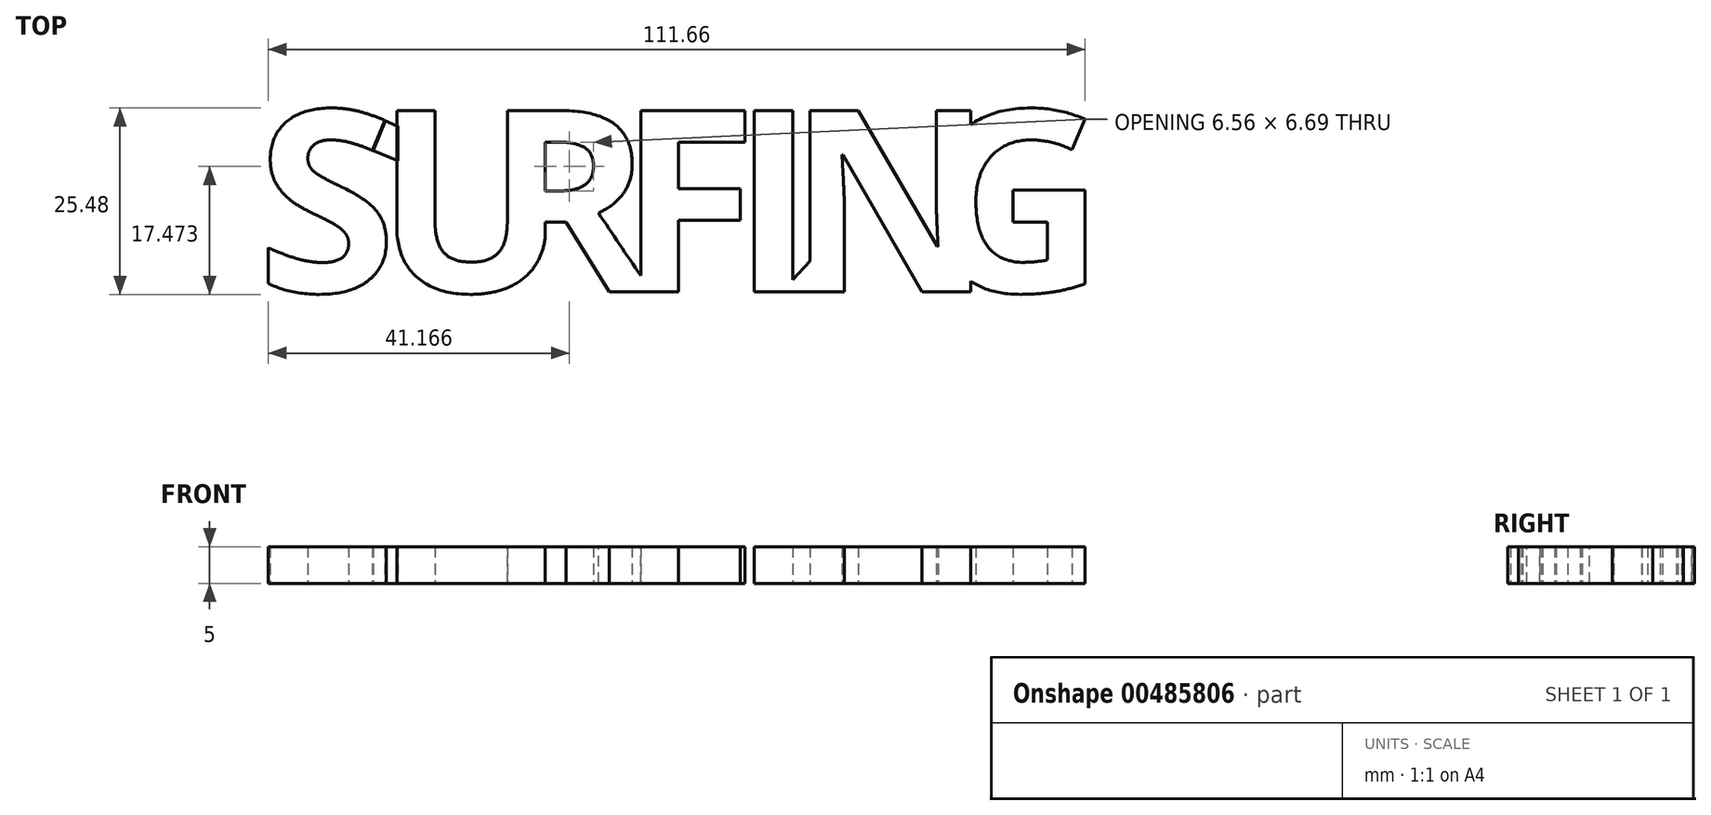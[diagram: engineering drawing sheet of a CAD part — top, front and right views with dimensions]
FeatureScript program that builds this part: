
annotation { "Feature Type Name" : "Feature", "Feature Type Description" : "" }
export const myFeature = defineFeature(function(context is Context, id is Id, definition is map)
    precondition{}
    {
        {
            var Q0;
            Q0=qCreatedBy(makeId("Top.planeOp"),FACE);
            var sketch = newSketch(context, id + "F0", { "sketchPlane" : qUnion([Q0])});
            skText(sketch, "E0", { "text": "S", "fontName": "NotoSans-Bold.ttf"});
            skText(sketch, "E1", { "text": "U", "fontName": "OpenSans-Bold.ttf"});
            skText(sketch, "E2", { "text": "R", "fontName": "OpenSans-Bold.ttf"});
            skText(sketch, "E3", { "text": "F", "fontName": "OpenSans-Bold.ttf"});
            skText(sketch, "E4", { "text": "I", "fontName": "OpenSans-Bold.ttf"});
            skText(sketch, "E5", { "text": "N", "fontName": "OpenSans-Bold.ttf"});
            skText(sketch, "E6", { "text": "G", "fontName": "OpenSans-Bold.ttf"});
            skLineSegment(sketch, "E7", {"start": v(-42.43, 23.41) * mm, "end": v(-40.7, 22.65) * mm});
            skLineSegment(sketch, "E8", {"start": v(-40.7, 22.65) * mm, "end": v(-40.7, 17.93) * mm});
            skLineSegment(sketch, "E9", {"start": v(-40.7, 17.93) * mm, "end": v(-44.15, 19.35) * mm});
            skLineSegment(sketch, "E10", {"start": v(-44.15, 19.35) * mm, "end": v(-42.43, 23.41) * mm});
            skLineSegment(sketch, "E11", {"start": v(6.74, 24.79) * mm, "end": v(10.2, 24.79) * mm});
            skLineSegment(sketch, "E12", {"start": v(10.2, 24.79) * mm, "end": v(6.74, 20.48) * mm});
            skLineSegment(sketch, "E13", {"start": v(6.74, 20.48) * mm, "end": v(6.74, 24.79) * mm});
            skLineSegment(sketch, "E14", {"start": v(15.66, 4.2) * mm, "end": v(11.68, 0) * mm});
            skLineSegment(sketch, "E15", {"start": v(11.68, 0) * mm, "end": v(16.34, 0) * mm});
            skLineSegment(sketch, "E16", {"start": v(16.34, 0) * mm, "end": v(20.31, 4.2) * mm});
            skLineSegment(sketch, "E17", {"start": v(20.31, 4.2) * mm, "end": v(15.66, 4.2) * mm});
            const initialGuessF0  = {"E0": [-0.06, 0, 1, 0, 0.025], "E1": [-0.04377, 0, 1, 0, 0.025], "E2": [-0.02889, 0, 1, 0, 0.025], "E3": [-0.0106, 0, 1, 0, 0.025], "E4": [0.00489, 0, 1, 0, 0.025], "E5": [0.01252, 0, 1, 0, 0.025], "E6": [0.0309, 0, 1, 0, 0.025]};
            skSetInitialGuess(sketch, initialGuessF0);
            skSolve(sketch);
        }
        {
            var Q0;
            Q0=makeQuery(id+"F0.imprint","IMPRINT",FACE,{"disambiguationData":[TD([[makeQuery(id+"F0.imprint","IMPRINT",EDGE,{"derivedFrom":sQuery(id+"F0.wireOp",EDGE,"E0.sketch_text.stroke-0")}),-1.0]])]});
            var Q1;
            {var subQ0=sQuery(id+"F0.wireOp",EDGE,"E7");var subQ1=sQuery(id+"F0.wireOp",EDGE,"E0.sketch_text.stroke-18");var subQ2=makeQuery(id+"F0.imprint","INTERSECT",VERTEX,{"derivedFrom":[subQ1,subQ0]});Q1=makeQuery(id+"F0.imprint","IMPRINT",FACE,{"disambiguationData":[TD([[makeQuery(id+"F0.imprint","IMPRINT",EDGE,{"disambiguationData":[TD([[subQ2,-1.0]])],"derivedFrom":subQ1}),1.0]])]});}
            var Q2;
            {var subQ6=sQuery(id+"F0.wireOp",EDGE,"E1.sketch_text.stroke-4");Q2=makeQuery(id+"F0.imprint","IMPRINT",FACE,{"disambiguationData":[TD([[makeQuery(id+"F0.imprint","IMPRINT",EDGE,{"derivedFrom":subQ6}),-1.0]])]});}
            var Q3;
            {var subQ2=sQuery(id+"F0.wireOp",EDGE,"E1.sketch_text.stroke-2");Q3=makeQuery(id+"F0.imprint","IMPRINT",FACE,{"disambiguationData":[TD([[makeQuery(id+"F0.imprint","IMPRINT",EDGE,{"derivedFrom":subQ2}),-1.0]])]});}
            var Q4;
            {var subQ12=sQuery(id+"F0.wireOp",EDGE,"E2.sketch_text.stroke-1");Q4=makeQuery(id+"F0.imprint","IMPRINT",FACE,{"disambiguationData":[TD([[makeQuery(id+"F0.imprint","IMPRINT",EDGE,{"derivedFrom":subQ12}),-1.0]])]});}
            var Q5;
            {var subQ9=sQuery(id+"F0.wireOp",EDGE,"E3.sketch_text.stroke-2");Q5=makeQuery(id+"F0.imprint","IMPRINT",FACE,{"disambiguationData":[TD([[makeQuery(id+"F0.imprint","IMPRINT",EDGE,{"derivedFrom":subQ9}),-1.0]])]});}
            var Q6;
            {var subQ0=sQuery(id+"F0.wireOp",EDGE,"E3.sketch_text.stroke-0");var subQ1=sQuery(id+"F0.wireOp",EDGE,"E2.sketch_text.stroke-15");var subQ2=makeQuery(id+"F0.imprint","INTERSECT",VERTEX,{"derivedFrom":[subQ1,subQ0]});Q6=makeQuery(id+"F0.imprint","IMPRINT",FACE,{"disambiguationData":[TD([[makeQuery(id+"F0.imprint","IMPRINT",EDGE,{"disambiguationData":[TD([[subQ2,1.0]])],"derivedFrom":subQ1}),-1.0]])]});}
            var Q7;
            {var subQ0=sQuery(id+"F0.wireOp",EDGE,"E11");var subQ1=sQuery(id+"F0.wireOp",EDGE,"E3.sketch_text.stroke-3");var subQ2=makeQuery(id+"F0.imprint","INTERSECT",VERTEX,{"derivedFrom":[subQ1,subQ0]});Q7=makeQuery(id+"F0.imprint","IMPRINT",FACE,{"disambiguationData":[TD([[makeQuery(id+"F0.imprint","IMPRINT",EDGE,{"disambiguationData":[TD([[subQ2,-1.0]])],"derivedFrom":subQ1}),1.0]])]});}
            var Q8;
            {var subQ1=sQuery(id+"F0.wireOp",EDGE,"E4.sketch_text.stroke-1");Q8=makeQuery(id+"F0.imprint","IMPRINT",FACE,{"disambiguationData":[TD([[makeQuery(id+"F0.imprint","IMPRINT",EDGE,{"derivedFrom":subQ1}),-1.0]])]});}
            var Q9;
            {var subQ0=sQuery(id+"F0.wireOp",EDGE,"E11");var subQ1=sQuery(id+"F0.wireOp",EDGE,"E4.sketch_text.stroke-0");var subQ2=makeQuery(id+"F0.imprint","INTERSECT",VERTEX,{"derivedFrom":[subQ1,subQ0]});Q9=makeQuery(id+"F0.imprint","IMPRINT",FACE,{"disambiguationData":[TD([[makeQuery(id+"F0.imprint","IMPRINT",EDGE,{"disambiguationData":[TD([[subQ2,1.0]])],"derivedFrom":subQ1}),-1.0]])]});}
            var Q10;
            {var subQ0=sQuery(id+"F0.wireOp",EDGE,"E15");var subQ1=sQuery(id+"F0.wireOp",EDGE,"E4.sketch_text.stroke-2");var subQ2=makeQuery(id+"F0.imprint","INTERSECT",VERTEX,{"derivedFrom":[subQ1,subQ0]});Q10=makeQuery(id+"F0.imprint","IMPRINT",FACE,{"disambiguationData":[TD([[makeQuery(id+"F0.imprint","IMPRINT",EDGE,{"disambiguationData":[TD([[subQ2,1.0]])],"derivedFrom":subQ1}),1.0]])]});}
            var Q11;
            {var subQ0=sQuery(id+"F0.wireOp",EDGE,"E15");var subQ1=sQuery(id+"F0.wireOp",EDGE,"E4.sketch_text.stroke-2");var subQ2=makeQuery(id+"F0.imprint","INTERSECT",VERTEX,{"derivedFrom":[subQ1,subQ0]});Q11=makeQuery(id+"F0.imprint","IMPRINT",FACE,{"disambiguationData":[TD([[makeQuery(id+"F0.imprint","IMPRINT",EDGE,{"disambiguationData":[TD([[subQ2,1.0]])],"derivedFrom":subQ1}),-1.0]])]});}
            var Q12;
            {var subQ0=sQuery(id+"F0.wireOp",EDGE,"E16");Q12=makeQuery(id+"F0.imprint","IMPRINT",FACE,{"disambiguationData":[TD([[makeQuery(id+"F0.imprint","IMPRINT",EDGE,{"derivedFrom":subQ0}),1.0]])]});}
            var Q13;
            {var subQ5=sQuery(id+"F0.wireOp",EDGE,"E5.sketch_text.stroke-0");Q13=makeQuery(id+"F0.imprint","IMPRINT",FACE,{"disambiguationData":[TD([[makeQuery(id+"F0.imprint","IMPRINT",EDGE,{"derivedFrom":subQ5}),-1.0]])]});}
            var Q14;
            Q14=makeQuery(id+"F0.imprint","IMPRINT",FACE,{"disambiguationData":[TD([[makeQuery(id+"F0.imprint","IMPRINT",EDGE,{"derivedFrom":sQuery(id+"F0.wireOp",EDGE,"E6.sketch_text.stroke-0")}),-1.0]])]});
            var Q15;
            {var subQ1=sQuery(id+"F0.wireOp",EDGE,"E6.sketch_text.stroke-5");Q15=makeQuery(id+"F0.imprint","IMPRINT",FACE,{"disambiguationData":[TD([[makeQuery(id+"F0.imprint","IMPRINT",EDGE,{"derivedFrom":subQ1}),-1.0]])]});}
            extrude(context, id + "F1", {"entities" : qUnion([Q0, Q1, Q2, Q3, Q4, Q5, Q6, Q7, Q8, Q9, Q10, Q11, Q12, Q13, Q14, Q15]), "depth" : 5 * mm});
        }
    });
